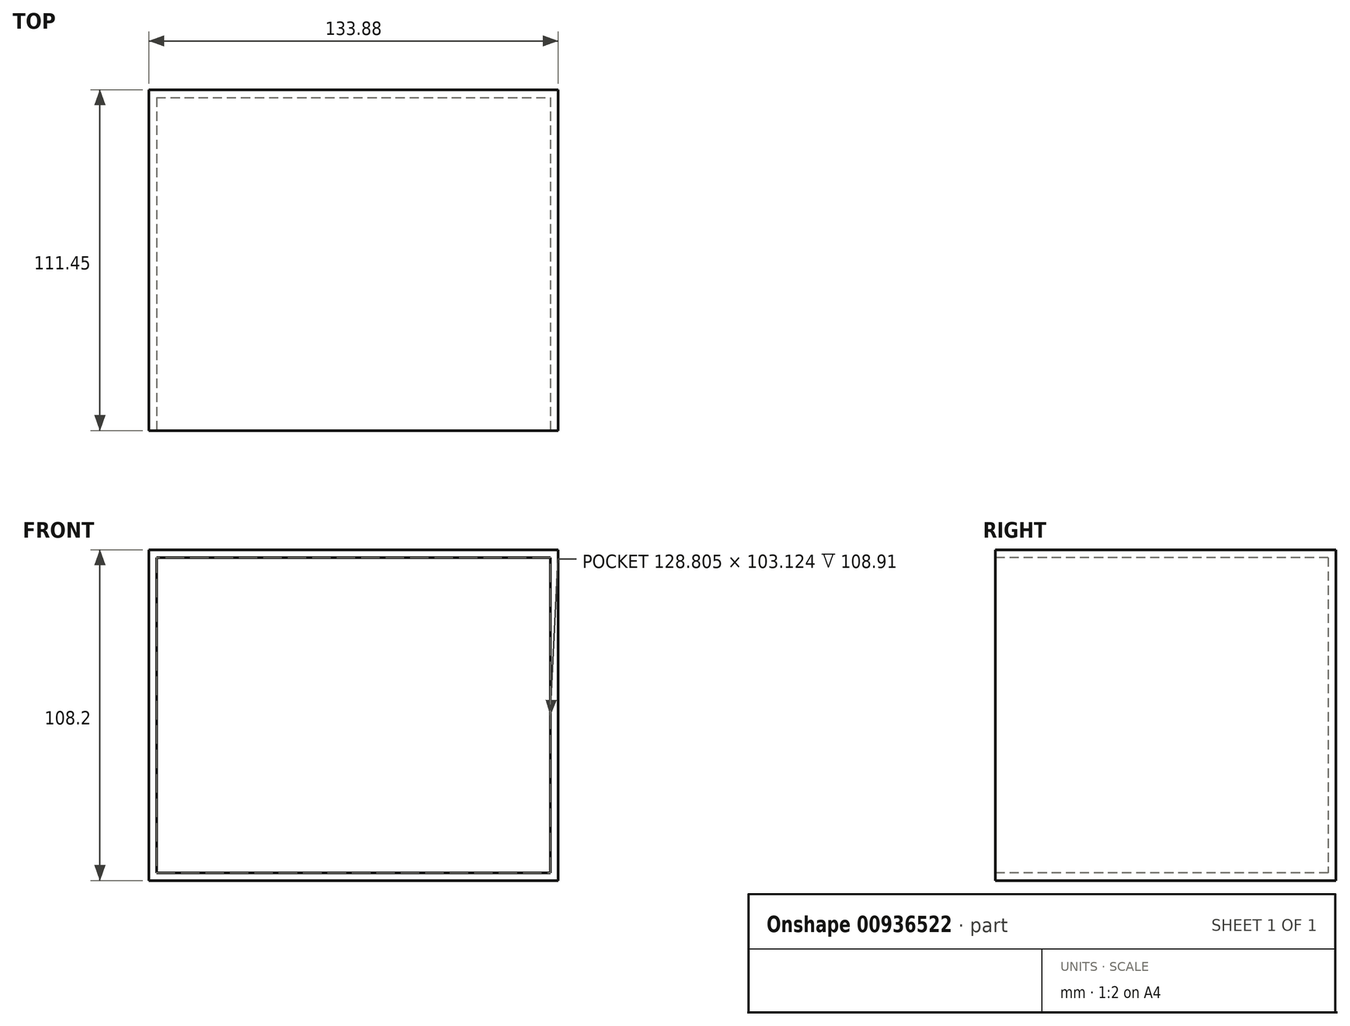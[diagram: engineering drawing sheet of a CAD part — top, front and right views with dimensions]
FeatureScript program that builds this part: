
annotation { "Feature Type Name" : "Feature", "Feature Type Description" : "" }
export const myFeature = defineFeature(function(context is Context, id is Id, definition is map)
    precondition{}
    {
        {
            var Q0;
            Q0=qCreatedBy(makeId("Top.planeOp"),FACE);
            var sketch = newSketch(context, id + "F0", { "sketchPlane" : qUnion([Q0])});
            skLineSegment(sketch, "E0.bottom", {"start": v(-62.65, 46.07) * mm, "end": v(66.15, 46.07) * mm});
            skLineSegment(sketch, "E0.top", {"start": v(-62.65, -62.84) * mm, "end": v(66.15, -62.84) * mm});
            skLineSegment(sketch, "E0.left", {"start": v(-62.65, 46.07) * mm, "end": v(-62.65, -62.84) * mm});
            skLineSegment(sketch, "E0.right", {"start": v(66.15, 46.07) * mm, "end": v(66.15, -62.84) * mm});
            skSolve(sketch);
        }
        {
            var Q0;
            Q0=makeQuery(id+"F0.imprint","IMPRINT",FACE,{"disambiguationData":[TD([[makeQuery(id+"F0.imprint","IMPRINT",EDGE,{"derivedFrom":sQuery(id+"F0.wireOp",EDGE,"E0.bottom")}),-1.0]])]});
            extrude(context, id + "F1", {"entities" : qUnion([Q0]), "depth" : 103.12 * mm, "offsetDistance" : 25.4 * mm});
        }
        {
            var Q0;
            Q0=makeQuery(id+"F1.opExtrude","SWEPT_FACE",FACE,{"disambiguationData":[OSD([sQuery(id+"F0.wireOp",EDGE,"E0.top")])]});
            shell(context, id + "F2", {"entities" : qUnion([Q0]), "thickness" : 2.54 * mm, "oppositeDirection" : true});
        }
    });
